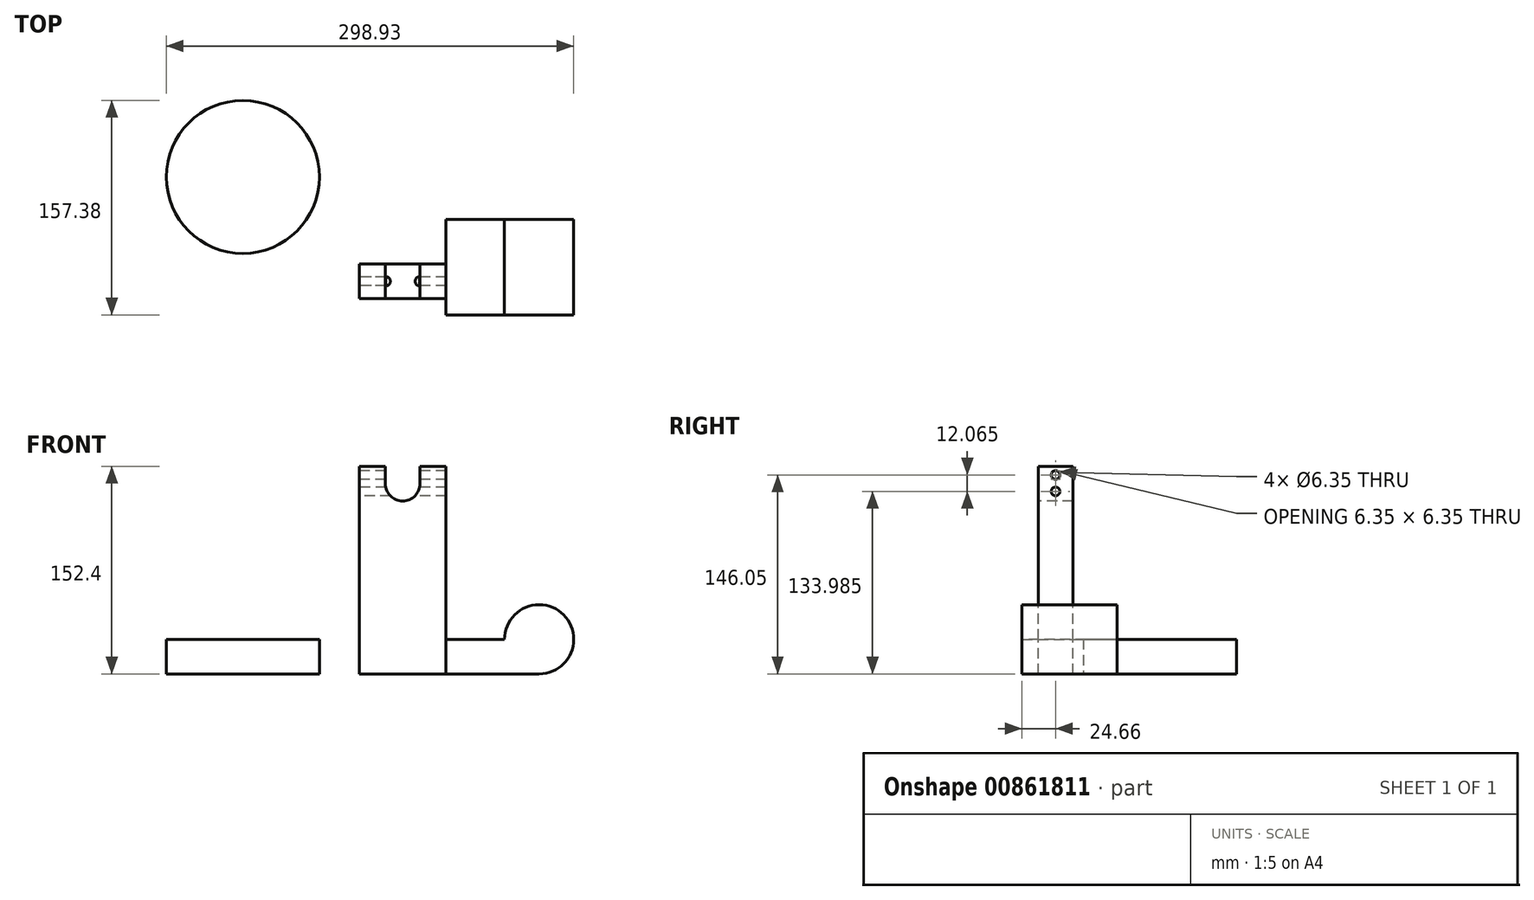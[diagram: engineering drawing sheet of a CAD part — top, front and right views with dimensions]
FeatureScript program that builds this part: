
annotation { "Feature Type Name" : "Feature", "Feature Type Description" : "" }
export const myFeature = defineFeature(function(context is Context, id is Id, definition is map)
    precondition{}
    {
        {
            var Q0;
            Q0=qCreatedBy(makeId("Front.planeOp"),FACE);
            var sketch = newSketch(context, id + "F0", { "sketchPlane" : qUnion([Q0])});
            skLineSegment(sketch, "E0.bottom", {"start": v(0, 0) * mm, "end": v(-63.5, 0) * mm});
            skLineSegment(sketch, "E0.top", {"start": v(0, 152.4) * mm, "end": v(-63.5, 152.4) * mm});
            skLineSegment(sketch, "E0.left", {"start": v(0, 0) * mm, "end": v(0, 152.4) * mm});
            skLineSegment(sketch, "E0.right", {"start": v(-63.5, 0) * mm, "end": v(-63.5, 152.4) * mm});
            skSolve(sketch);
        }
        {
            var Q0;
            Q0 = qSketchRegion(id + "F0", true);
            extrude(context, id + "F1", {"entities" : qUnion([Q0]), "depth" : 25.4 * mm, "offsetDistance" : 25.4 * mm});
        }
        {
            var Q0;
            Q0=makeQuery(id+"F1.opExtrude","CAP_FACE",FACE,{"disambiguationData":[OSD([sQuery(id+"F0.wireOp",EDGE,"E0.bottom"),sQuery(id+"F0.wireOp",EDGE,"E0.top"),sQuery(id+"F0.wireOp",EDGE,"E0.left"),sQuery(id+"F0.wireOp",EDGE,"E0.right")])],"isStart":false});
            var sketch = newSketch(context, id + "F2", { "sketchPlane" : qUnion([Q0])});
            skLineSegment(sketch, "E1", {"start": v(-31.75, 152.4) * mm, "end": v(-31.75, 0) * mm, "construction": true});
            skCircle(sketch, "E2", {"center": v(-31.75, 139.7) * mm, "radius": 12.7 * mm});
            skLineSegment(sketch, "E3", {"start": v(-63.5, 139.7) * mm, "end": v(0, 139.7) * mm, "construction": true});
            skLineSegment(sketch, "E4", {"start": v(-44.45, 139.7) * mm, "end": v(-44.45, 152.4) * mm});
            skLineSegment(sketch, "E5", {"start": v(-19.05, 139.7) * mm, "end": v(-19.05, 152.4) * mm});
            skSolve(sketch);
        }
        {
            var Q0;
            {var subQ0=sQuery(id+"F2.wireOp",EDGE,"E2");var subQ1=makeQuery(id+"F2.imprint","INTERSECT",VERTEX,{"derivedFrom":[subQ0,sQuery(id+"F2.wireOp",EDGE,"E5")]});Q0=makeQuery(id+"F2.imprint","IMPRINT",FACE,{"disambiguationData":[TD([[makeQuery(id+"F2.imprint","IMPRINT",EDGE,{"disambiguationData":[TD([[subQ1,-1.0]])],"derivedFrom":subQ0}),1.0]])]});}
            var Q1;
            {var subQ0=sQuery(id+"F2.wireOp",EDGE,"E4");Q1=makeQuery(id+"F2.imprint","IMPRINT",FACE,{"disambiguationData":[TD([[makeQuery(id+"F2.imprint","IMPRINT",EDGE,{"derivedFrom":subQ0}),-1.0]])]});}
            var Q2;
            {var subQ0=sQuery(id+"F2.wireOp",EDGE,"E5");Q2=makeQuery(id+"F2.imprint","IMPRINT",FACE,{"disambiguationData":[TD([[makeQuery(id+"F2.imprint","IMPRINT",EDGE,{"derivedFrom":subQ0}),1.0]])]});}
            extrude(context, id + "F3", {"entities" : qUnion([Q0, Q1, Q2]), "operationType" : NewBodyOperationType.REMOVE, "oppositeDirection" : true, "depth" : 25.4 * mm, "offsetDistance" : 25.4 * mm});
        }
        {
            var Q0;
            Q0=makeQuery(id+"F1.opExtrude","SWEPT_FACE",FACE,{"disambiguationData":[OSD([sQuery(id+"F0.wireOp",EDGE,"E0.right")])]});
            var sketch = newSketch(context, id + "F4", { "sketchPlane" : qUnion([Q0])});
            skLineSegment(sketch, "E6", {"start": v(12.7, 152.4) * mm, "end": v(12.7, 0) * mm, "construction": true});
            skCircle(sketch, "E7", {"center": v(12.7, 133.99) * mm, "radius": 3.18 * mm});
            skCircle(sketch, "E8", {"center": v(12.7, 146.05) * mm, "radius": 3.17 * mm});
            skSolve(sketch);
        }
        {
            var Q0;
            Q0 = qSketchRegion(id + "F4", true);
            extrude(context, id + "F5", {"entities" : qUnion([Q0]), "operationType" : NewBodyOperationType.REMOVE, "endBound" : BoundingType.THROUGH_ALL, "oppositeDirection" : true, "depth" : 25.4 * mm, "offsetDistance" : 25.4 * mm});
        }
        {
            var Q0;
            Q0=qCreatedBy(makeId("Top.planeOp"),FACE);
            var sketch = newSketch(context, id + "F6", { "sketchPlane" : qUnion([Q0])});
            skLineSegment(sketch, "E9.bottom", {"start": v(68.31, -37.36) * mm, "end": v(0, -37.36) * mm});
            skLineSegment(sketch, "E9.top", {"start": v(68.31, 32.64) * mm, "end": v(0, 32.64) * mm});
            skLineSegment(sketch, "E9.left", {"start": v(68.31, -37.36) * mm, "end": v(68.31, 32.64) * mm});
            skLineSegment(sketch, "E9.right", {"start": v(0, -37.36) * mm, "end": v(0, 32.64) * mm});
            skSolve(sketch);
        }
        {
            var Q0;
            Q0 = qSketchRegion(id + "F6", true);
            extrude(context, id + "F7", {"entities" : qUnion([Q0]), "operationType" : NewBodyOperationType.ADD, "depth" : 25.4 * mm, "offsetDistance" : 25.4 * mm});
        }
        {
            var Q0;
            Q0=makeQuery(id+"F7.opExtrude","SWEPT_FACE",FACE,{"disambiguationData":[OSD([sQuery(id+"F6.wireOp",EDGE,"E9.left")])]});
            var Q1;
            Q1=makeQuery(id+"F7.opExtrude","CAP_EDGE",EDGE,{"disambiguationData":[OSD([sQuery(id+"F6.wireOp",EDGE,"E9.left")])],"isStart":false});
            revolve(context, id + "F8", {"operationType" : NewBodyOperationType.ADD, "surfaceOperationType" : NewSurfaceOperationType.NEW, "entities" : qUnion([Q0]), "axis" : qUnion([Q1]), "revolveType" : RevolveType.FULL});
        }
        {
            var Q0;
            Q0=qCreatedBy(makeId("Top.planeOp"),FACE);
            var sketch = newSketch(context, id + "F9", { "sketchPlane" : qUnion([Q0])});
            skCircle(sketch, "E10", {"center": v(-149.09, 63.9) * mm, "radius": 56.13 * mm});
            skSolve(sketch);
        }
        {
            var Q0;
            Q0=makeQuery(id+"F9.imprint","IMPRINT",FACE,{"disambiguationData":[TD([[makeQuery(id+"F9.imprint","IMPRINT",EDGE,{"derivedFrom":sQuery(id+"F9.wireOp",EDGE,"E10")}),1.0]])]});
            extrude(context, id + "F10", {"entities" : qUnion([Q0]), "depth" : 25.4 * mm, "offsetDistance" : 25.4 * mm});
        }
    });
